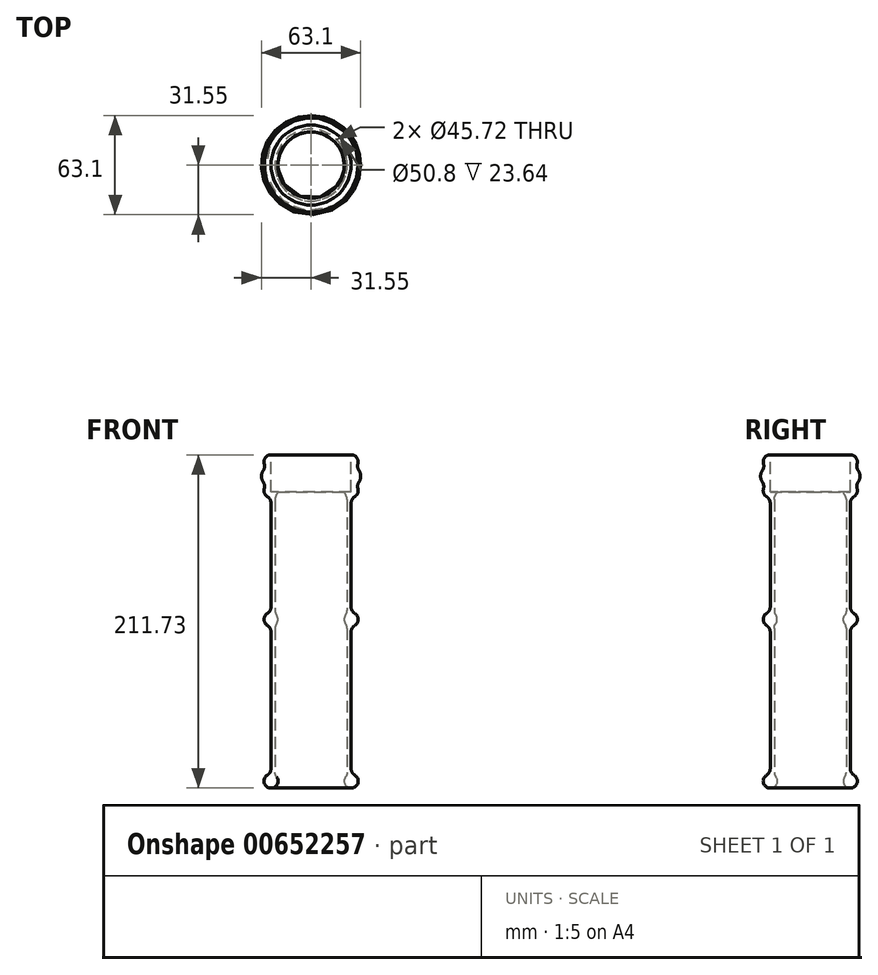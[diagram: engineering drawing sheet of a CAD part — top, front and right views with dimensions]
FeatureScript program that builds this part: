
annotation { "Feature Type Name" : "Feature", "Feature Type Description" : "" }
export const myFeature = defineFeature(function(context is Context, id is Id, definition is map)
    precondition{}
    {
        {
            var Q0;
            Q0=qCreatedBy(makeId("Top.planeOp"),FACE);
            var sketch = newSketch(context, id + "F0", { "sketchPlane" : qUnion([Q0])});
            skCircle(sketch, "E0", {"center": v(0, 0) * mm, "radius": 25.4 * mm});
            skCircle(sketch, "E1", {"center": v(0, 0) * mm, "radius": 22.86 * mm});
            skSolve(sketch);
        }
        {
            var Q0;
            Q0=makeQuery(id+"F0.imprint","IMPRINT",FACE,{"disambiguationData":[TD([[makeQuery(id+"F0.imprint","IMPRINT",EDGE,{"derivedFrom":sQuery(id+"F0.wireOp",EDGE,"E0")}),1.0]])]});
            extrude(context, id + "F1", {"entities" : qUnion([Q0]), "depth" : 203.2 * mm, "offsetDistance" : 25.4 * mm});
        }
        {
            var Q0;
            Q0=qCreatedBy(makeId("Front.planeOp"),FACE);
            var sketch = newSketch(context, id + "F2", { "sketchPlane" : qUnion([Q0])});
            skCircle(sketch, "E2", {"center": v(-25.46, 0) * mm, "radius": 4.45 * mm});
            skCircle(sketch, "E3", {"center": v(-25.46, 102.73) * mm, "radius": 4.45 * mm});
            skCircle(sketch, "E4", {"center": v(-25.46, 202.84) * mm, "radius": 4.45 * mm});
            skCircle(sketch, "E5", {"center": v(-25.2, 193.67) * mm, "radius": 6.35 * mm});
            skCircle(sketch, "E6", {"center": v(-25.48, 184.51) * mm, "radius": 4.45 * mm});
            skSolve(sketch);
        }
        {
            var Q0;
            Q0 = qSketchRegion(id + "F2", true);
            var Q1;
            Q1=makeQuery(id+"F1.opExtrude","SWEPT_FACE",FACE,{"disambiguationData":[OSD([sQuery(id+"F0.wireOp",EDGE,"E0")])]});
            revolve(context, id + "F3", {"operationType" : NewBodyOperationType.ADD, "entities" : qUnion([Q0]), "axis" : qUnion([Q1]), "revolveType" : RevolveType.FULL});
        }
        {
            var Q0;
            Q0=makeQuery(id+"F3.opRevolve","SWEPT_FACE",FACE,{"disambiguationData":[OSD([sQuery(id+"F2.wireOp",EDGE,"E2")])]});
            var Q1;
            Q1=makeQuery(id+"F3.boolean.opBoolean","SPLIT",FACE,{"disambiguationData":[TD([makeQuery(id+"F3.opRevolve","SWEPT_FACE",FACE,{"disambiguationData":[OSD([sQuery(id+"F2.wireOp",EDGE,"E6")])]})])],"derivedFrom":makeQuery(id+"F1.opExtrude","SWEPT_FACE",FACE,{"disambiguationData":[OSD([sQuery(id+"F0.wireOp",EDGE,"E0")])]})});
            var Q2;
            Q2=makeQuery(id+"F3.boolean.opBoolean","SPLIT",FACE,{"disambiguationData":[TD([makeQuery(id+"F1.opExtrude","SWEPT_FACE",FACE,{"disambiguationData":[OSD([sQuery(id+"F0.wireOp",EDGE,"E0")])]})])],"derivedFrom":makeQuery(id+"F3.opRevolve","SWEPT_FACE",FACE,{"disambiguationData":[OSD([sQuery(id+"F2.wireOp",EDGE,"E3")])]})});
            var Q3;
            Q3=makeQuery(id+"F3.opRevolve","SWEPT_FACE",FACE,{"disambiguationData":[OSD([sQuery(id+"F2.wireOp",EDGE,"E4")])]});
            var Q4;
            Q4=makeQuery(id+"F3.boolean.opBoolean","SPLIT",FACE,{"disambiguationData":[TD([makeQuery(id+"F3.opRevolve","SWEPT_FACE",FACE,{"disambiguationData":[OSD([sQuery(id+"F2.wireOp",EDGE,"E2")])]})])],"derivedFrom":makeQuery(id+"F1.opExtrude","SWEPT_FACE",FACE,{"disambiguationData":[OSD([sQuery(id+"F0.wireOp",EDGE,"E0")])]})});
            var Q5;
            {var subQ0=sQuery(id+"F2.wireOp",EDGE,"E5");Q5=makeQuery(id+"F3.opRevolve","SWEPT_FACE",FACE,{"disambiguationData":[OSD([subQ0]),TDD([makeQuery(id+"F2.imprint","IMPRINT",EDGE,{"disambiguationData":[TD([[makeQuery(id+"F2.imprint","INTERSECT",VERTEX,{"disambiguationData":[OD(0.0)],"derivedFrom":[sQuery(id+"F2.wireOp",EDGE,"E4"),subQ0]}),-1.0]])],"derivedFrom":subQ0})])]});}
            var Q6;
            {var subQ1=sQuery(id+"F2.wireOp",EDGE,"E6");Q6=makeQuery(id+"F3.boolean.opBoolean","SPLIT",FACE,{"disambiguationData":[TD([makeQuery(id+"F1.opExtrude","SWEPT_FACE",FACE,{"disambiguationData":[OSD([sQuery(id+"F0.wireOp",EDGE,"E0")])]})])],"derivedFrom":makeQuery(id+"F3.opRevolve","SWEPT_FACE",FACE,{"disambiguationData":[OSD([subQ1])]})});}
            var Q7;
            Q7=makeQuery(id+"F3.boolean.opBoolean","SPLIT",FACE,{"disambiguationData":[TD([makeQuery(id+"F3.opRevolve","SWEPT_FACE",FACE,{"disambiguationData":[OSD([sQuery(id+"F2.wireOp",EDGE,"E6")])]})])],"derivedFrom":makeQuery(id+"F1.opExtrude","SWEPT_FACE",FACE,{"disambiguationData":[OSD([sQuery(id+"F0.wireOp",EDGE,"E1")])]})});
            var Q8;
            {var subQ0=sQuery(id+"F2.wireOp",EDGE,"E6");var subQ1=sQuery(id+"F2.wireOp",EDGE,"E5");Q8=makeQuery(id+"F3.opRevolve","SWEPT_EDGE",EDGE,{"disambiguationData":[OSD([subQ1,subQ0]),TDD([makeQuery(id+"F2.imprint","INTERSECT",VERTEX,{"disambiguationData":[OD(0.0)],"derivedFrom":[subQ1,subQ0]})])]});}
            var Q9;
            {var subQ1=sQuery(id+"F2.wireOp",EDGE,"E6");Q9=makeQuery(id+"F3.boolean.opBoolean","SPLIT",FACE,{"disambiguationData":[TD([makeQuery(id+"F1.opExtrude","SWEPT_FACE",FACE,{"disambiguationData":[OSD([sQuery(id+"F0.wireOp",EDGE,"E1")])]})])],"derivedFrom":makeQuery(id+"F3.opRevolve","SWEPT_FACE",FACE,{"disambiguationData":[OSD([subQ1])]})});}
            var Q10;
            Q10=makeQuery(id+"F3.boolean.opBoolean","INTERSECT",EDGE,{"derivedFrom":[makeQuery(id+"F1.opExtrude","SWEPT_FACE",FACE,{"disambiguationData":[OSD([sQuery(id+"F0.wireOp",EDGE,"E0")])]}),makeQuery(id+"F3.opRevolve","SWEPT_FACE",FACE,{"disambiguationData":[OSD([sQuery(id+"F2.wireOp",EDGE,"E2")])]})]});
            var Q11;
            Q11=makeQuery(id+"F3.boolean.opBoolean","INTERSECT",EDGE,{"disambiguationData":[OD(0.0)],"derivedFrom":[makeQuery(id+"F1.opExtrude","SWEPT_FACE",FACE,{"disambiguationData":[OSD([sQuery(id+"F0.wireOp",EDGE,"E0")])]}),makeQuery(id+"F3.opRevolve","SWEPT_FACE",FACE,{"disambiguationData":[OSD([sQuery(id+"F2.wireOp",EDGE,"E3")])]})]});
            var Q12;
            {var subQ0=sQuery(id+"F2.wireOp",EDGE,"E5");var subQ1=sQuery(id+"F2.wireOp",EDGE,"E4");Q12=makeQuery(id+"F3.opRevolve","SWEPT_EDGE",EDGE,{"disambiguationData":[OSD([subQ1,subQ0]),TDD([makeQuery(id+"F2.imprint","INTERSECT",VERTEX,{"disambiguationData":[OD(0.0)],"derivedFrom":[subQ1,subQ0]})])]});}
            var Q13;
            Q13=makeQuery(id+"F3.boolean.opBoolean","SPLIT",FACE,{"disambiguationData":[TD([makeQuery(id+"F3.opRevolve","SWEPT_FACE",FACE,{"disambiguationData":[OSD([sQuery(id+"F2.wireOp",EDGE,"E2")])]})])],"derivedFrom":makeQuery(id+"F1.opExtrude","SWEPT_FACE",FACE,{"disambiguationData":[OSD([sQuery(id+"F0.wireOp",EDGE,"E1")])]})});
            var Q14;
            Q14=makeQuery(id+"F3.boolean.opBoolean","INTERSECT",EDGE,{"derivedFrom":[makeQuery(id+"F1.opExtrude","SWEPT_FACE",FACE,{"disambiguationData":[OSD([sQuery(id+"F0.wireOp",EDGE,"E1")])]}),makeQuery(id+"F3.opRevolve","SWEPT_FACE",FACE,{"disambiguationData":[OSD([sQuery(id+"F2.wireOp",EDGE,"E6")])]})]});
            var Q15;
            Q15=makeQuery(id+"F3.boolean.opBoolean","INTERSECT",EDGE,{"disambiguationData":[OD(0.0)],"derivedFrom":[makeQuery(id+"F1.opExtrude","SWEPT_FACE",FACE,{"disambiguationData":[OSD([sQuery(id+"F0.wireOp",EDGE,"E1")])]}),makeQuery(id+"F3.opRevolve","SWEPT_FACE",FACE,{"disambiguationData":[OSD([sQuery(id+"F2.wireOp",EDGE,"E3")])]})]});
            var Q16;
            Q16=makeQuery(id+"F3.boolean.opBoolean","INTERSECT",EDGE,{"derivedFrom":[makeQuery(id+"F1.opExtrude","SWEPT_FACE",FACE,{"disambiguationData":[OSD([sQuery(id+"F0.wireOp",EDGE,"E1")])]}),makeQuery(id+"F3.opRevolve","SWEPT_FACE",FACE,{"disambiguationData":[OSD([sQuery(id+"F2.wireOp",EDGE,"E2")])]})]});
            var Q17;
            Q17=makeQuery(id+"F3.boolean.opBoolean","SPLIT",FACE,{"disambiguationData":[TD([makeQuery(id+"F1.opExtrude","SWEPT_FACE",FACE,{"disambiguationData":[OSD([sQuery(id+"F0.wireOp",EDGE,"E1")])]})])],"derivedFrom":makeQuery(id+"F3.opRevolve","SWEPT_FACE",FACE,{"disambiguationData":[OSD([sQuery(id+"F2.wireOp",EDGE,"E3")])]})});
            var Q18;
            Q18=makeQuery(id+"F3.boolean.opBoolean","INTERSECT",EDGE,{"derivedFrom":[makeQuery(id+"F1.opExtrude","SWEPT_FACE",FACE,{"disambiguationData":[OSD([sQuery(id+"F0.wireOp",EDGE,"E0")])]}),makeQuery(id+"F3.opRevolve","SWEPT_FACE",FACE,{"disambiguationData":[OSD([sQuery(id+"F2.wireOp",EDGE,"E6")])]})]});
            var Q19;
            {var subQ0=sQuery(id+"F2.wireOp",EDGE,"E5");Q19=makeQuery(id+"F3.opRevolve","SWEPT_FACE",FACE,{"disambiguationData":[OSD([subQ0]),TDD([makeQuery(id+"F2.imprint","IMPRINT",EDGE,{"disambiguationData":[TD([[makeQuery(id+"F2.imprint","INTERSECT",VERTEX,{"disambiguationData":[OD(1.0)],"derivedFrom":[sQuery(id+"F2.wireOp",EDGE,"E4"),subQ0]}),1.0]])],"derivedFrom":subQ0})])]});}
            var Q20;
            Q20=makeQuery(id+"F3.boolean.opBoolean","INTERSECT",EDGE,{"disambiguationData":[OD(1.0)],"derivedFrom":[makeQuery(id+"F1.opExtrude","SWEPT_FACE",FACE,{"disambiguationData":[OSD([sQuery(id+"F0.wireOp",EDGE,"E0")])]}),makeQuery(id+"F3.opRevolve","SWEPT_FACE",FACE,{"disambiguationData":[OSD([sQuery(id+"F2.wireOp",EDGE,"E3")])]})]});
            var Q21;
            {var subQ0=sQuery(id+"F2.wireOp",EDGE,"E6");var subQ1=sQuery(id+"F2.wireOp",EDGE,"E5");Q21=makeQuery(id+"F3.opRevolve","SWEPT_EDGE",EDGE,{"disambiguationData":[OSD([subQ1,subQ0]),TDD([makeQuery(id+"F2.imprint","INTERSECT",VERTEX,{"disambiguationData":[OD(1.0)],"derivedFrom":[subQ1,subQ0]})])]});}
            var Q22;
            Q22=makeQuery(id+"F3.boolean.opBoolean","INTERSECT",EDGE,{"disambiguationData":[OD(1.0)],"derivedFrom":[makeQuery(id+"F1.opExtrude","SWEPT_FACE",FACE,{"disambiguationData":[OSD([sQuery(id+"F0.wireOp",EDGE,"E1")])]}),makeQuery(id+"F3.opRevolve","SWEPT_FACE",FACE,{"disambiguationData":[OSD([sQuery(id+"F2.wireOp",EDGE,"E3")])]})]});
            var Q23;
            {var subQ0=sQuery(id+"F2.wireOp",EDGE,"E5");var subQ1=sQuery(id+"F2.wireOp",EDGE,"E4");Q23=makeQuery(id+"F3.opRevolve","SWEPT_EDGE",EDGE,{"disambiguationData":[OSD([subQ1,subQ0]),TDD([makeQuery(id+"F2.imprint","INTERSECT",VERTEX,{"disambiguationData":[OD(1.0)],"derivedFrom":[subQ1,subQ0]})])]});}
            fillet(context, id + "F4", {"entities" : qUnion([Q0, Q1, Q2, Q3, Q4, Q5, Q6, Q7, Q8, Q9, Q10, Q11, Q12, Q13, Q14, Q15, Q16, Q17, Q18, Q19, Q20, Q21, Q22, Q23]), "radius" : 5.08 * mm, "tangentPropagation" : true, "allowEdgeOverflow" : false});
        }
        {
            var Q0;
            Q0=qCreatedBy(makeId("Top.planeOp"),FACE);
            cPlane(context, id + "F5", {"entities" : qUnion([Q0]), "cplaneType" : CPlaneType.OFFSET, "offset" : 209.04 * mm, "width" : 152.4 * mm, "height" : 152.4 * mm});
        }
        {
            var Q0;
            Q0=qCreatedBy(id+"F5.planeOp",FACE);
            var sketch = newSketch(context, id + "F6", { "sketchPlane" : qUnion([Q0])});
            skCircle(sketch, "E7", {"center": v(0, 0) * mm, "radius": 25.4 * mm});
            skSolve(sketch);
        }
        {
            var Q0;
            Q0 = qSketchRegion(id + "F6", true);
            extrude(context, id + "F7", {"entities" : qUnion([Q0]), "operationType" : NewBodyOperationType.REMOVE, "oppositeDirection" : true, "depth" : 25.4 * mm, "offsetDistance" : 25.4 * mm});
        }
    });
